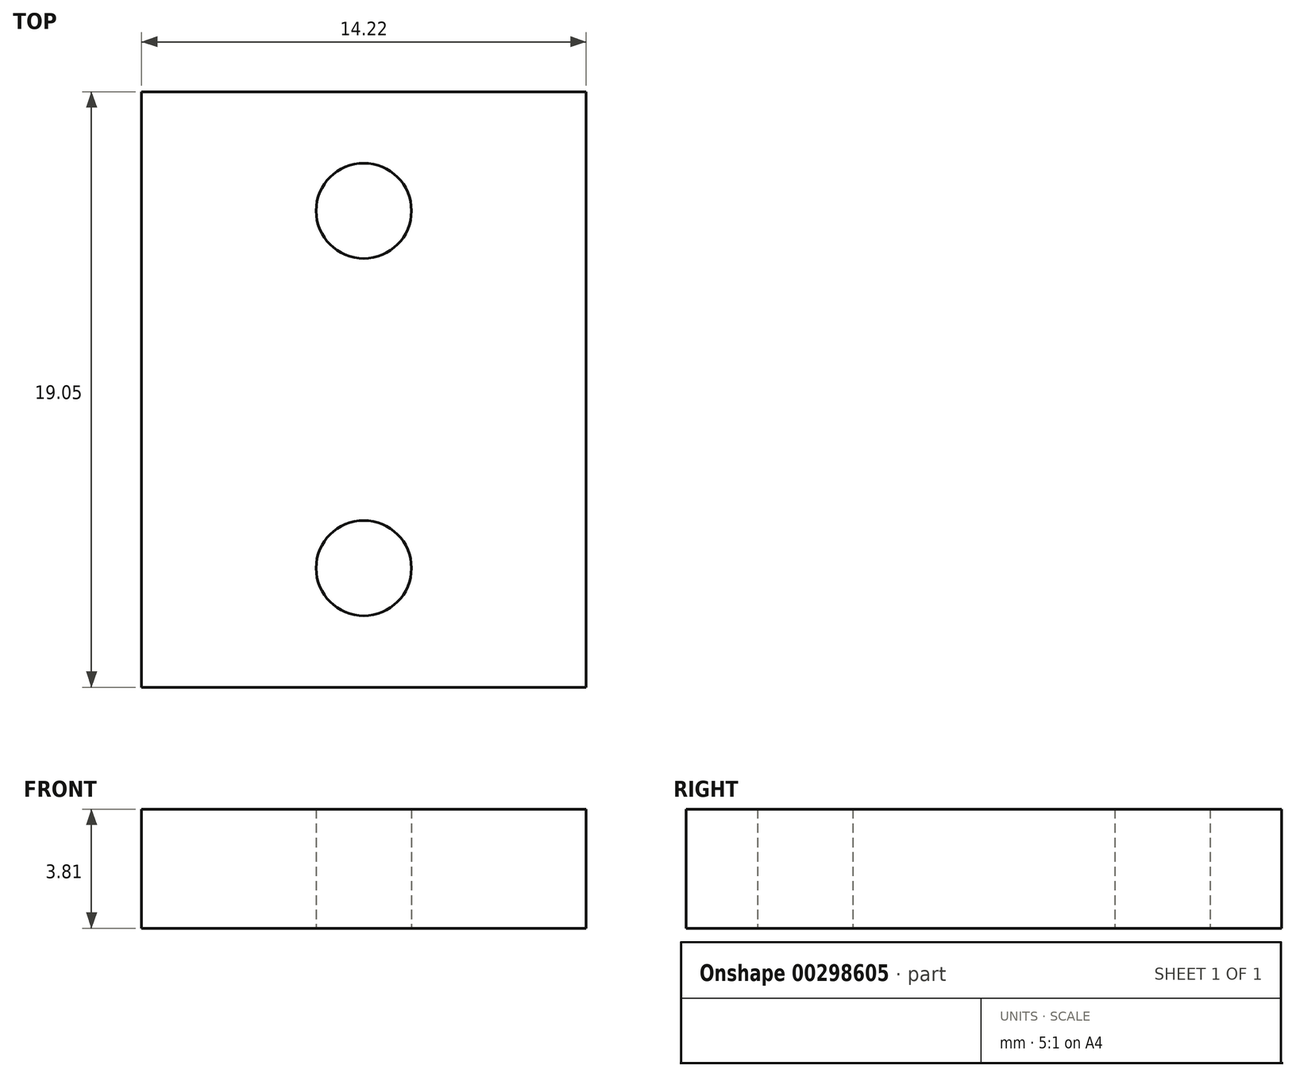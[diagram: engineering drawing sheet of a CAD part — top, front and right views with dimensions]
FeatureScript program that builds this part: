
annotation { "Feature Type Name" : "Feature", "Feature Type Description" : "" }
export const myFeature = defineFeature(function(context is Context, id is Id, definition is map)
    precondition{}
    {
        {
            var Q0;
            Q0=qCreatedBy(makeId("Top.planeOp"),FACE);
            var sketch = newSketch(context, id + "F0", { "sketchPlane" : qUnion([Q0])});
            skLineSegment(sketch, "E0.bottom", {"start": v(0, 0) * mm, "end": v(-14.22, 0) * mm});
            skLineSegment(sketch, "E0.top", {"start": v(0, 19.05) * mm, "end": v(-14.22, 19.05) * mm});
            skLineSegment(sketch, "E0.left", {"start": v(0, 0) * mm, "end": v(0, 19.05) * mm});
            skLineSegment(sketch, "E0.right", {"start": v(-14.22, 0) * mm, "end": v(-14.22, 19.05) * mm});
            skLineSegment(sketch, "E1", {"start": v(-7.11, 19.05) * mm, "end": v(-7.11, 16.76) * mm});
            skLineSegment(sketch, "E2", {"start": v(-7.11, 9.53) * mm, "end": v(0, 9.53) * mm});
            skCircle(sketch, "E3", {"center": v(-7.11, 15.24) * mm, "radius": 1.52 * mm});
            skCircle(sketch, "E4", {"center": v(-7.11, 3.8) * mm, "radius": 1.52 * mm});
            skLineSegment(sketch, "E5.trimOffspring", {"start": v(-7.11, 13.72) * mm, "end": v(-7.11, 5.33) * mm});
            skLineSegment(sketch, "E6.trimOffspring", {"start": v(-7.11, 2.29) * mm, "end": v(-7.11, 0) * mm});
            skPoint(sketch, "E7.orphan", {"position": v(-14.22, 9.53) * mm});
            skSolve(sketch);
        }
        {
            var Q0;
            {var subQ4=sQuery(id+"F0.wireOp",EDGE,"E1");Q0=makeQuery(id+"F0.imprint","IMPRINT",FACE,{"disambiguationData":[TD([[makeQuery(id+"F0.imprint","IMPRINT",EDGE,{"derivedFrom":subQ4}),1.0]])]});}
            var Q1;
            {var subQ1=sQuery(id+"F0.wireOp",EDGE,"E0.right");Q1=makeQuery(id+"F0.imprint","IMPRINT",FACE,{"disambiguationData":[TD([[makeQuery(id+"F0.imprint","IMPRINT",EDGE,{"derivedFrom":subQ1}),-1.0]])]});}
            var Q2;
            {var subQ4=sQuery(id+"F0.wireOp",EDGE,"E2");Q2=makeQuery(id+"F0.imprint","IMPRINT",FACE,{"disambiguationData":[TD([[makeQuery(id+"F0.imprint","IMPRINT",EDGE,{"derivedFrom":subQ4}),-1.0]])]});}
            extrude(context, id + "F1", {"entities" : qUnion([Q0, Q1, Q2]), "depth" : 3.8 * mm});
        }
    });
